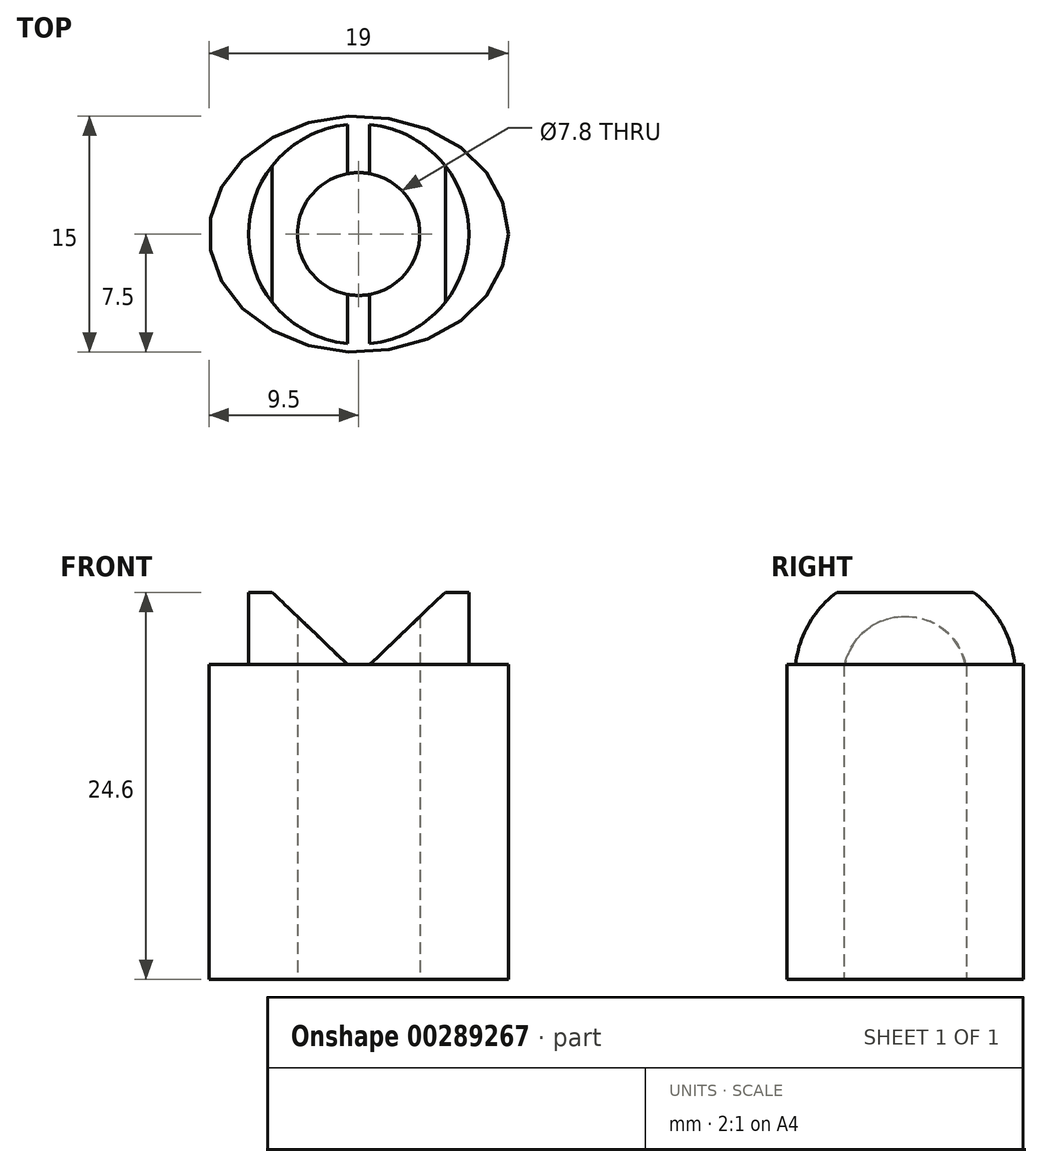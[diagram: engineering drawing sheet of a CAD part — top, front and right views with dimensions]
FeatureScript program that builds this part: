
annotation { "Feature Type Name" : "Feature", "Feature Type Description" : "" }
export const myFeature = defineFeature(function(context is Context, id is Id, definition is map)
    precondition{}
    {
        {
            var Q0;
            Q0=qCreatedBy(makeId("Top.planeOp"),FACE);
            var sketch = newSketch(context, id + "F0", { "sketchPlane" : qUnion([Q0])});
            skEllipse(sketch, "E0", {"center": v(0, 0) * mm, "majorRadius": 9.5 * mm, "minorRadius": 7.5 * mm, "majorAxis": v(1, 0)});
            skSolve(sketch);
        }
        {
            var Q0;
            Q0=makeQuery(id+"F0.imprint","IMPRINT",FACE,{"disambiguationData":[TD([[makeQuery(id+"F0.imprint","IMPRINT",EDGE,{"derivedFrom":sQuery(id+"F0.wireOp",EDGE,"E0")}),1.0]])]});
            extrude(context, id + "F1", {"entities" : qUnion([Q0]), "depth" : 20 * mm});
        }
        {
            var Q0;
            Q0=makeQuery(id+"F1.opExtrude","CAP_FACE",FACE,{"disambiguationData":[OSD([sQuery(id+"F0.wireOp",EDGE,"E0")])],"isStart":false});
            var sketch = newSketch(context, id + "F2", { "sketchPlane" : qUnion([Q0])});
            skCircle(sketch, "E1", {"center": v(0, 0) * mm, "radius": 7 * mm});
            skSolve(sketch);
        }
        {
            var Q0;
            Q0=makeQuery(id+"F2.imprint","IMPRINT",FACE,{"disambiguationData":[TD([[makeQuery(id+"F2.imprint","IMPRINT",EDGE,{"derivedFrom":sQuery(id+"F2.wireOp",EDGE,"E1")}),1.0]])]});
            extrude(context, id + "F3", {"entities" : qUnion([Q0]), "operationType" : NewBodyOperationType.ADD, "depth" : 4.6 * mm});
        }
        {
            var Q0;
            Q0=qCreatedBy(makeId("Front.planeOp"),FACE);
            var sketch = newSketch(context, id + "F4", { "sketchPlane" : qUnion([Q0])});
            skLineSegment(sketch, "E2.bottom", {"start": v(-0.7, 20) * mm, "end": v(0.7, 20) * mm});
            skLineSegment(sketch, "E2.top", {"start": v(-0.7, 24.6) * mm, "end": v(0.7, 24.6) * mm});
            skLineSegment(sketch, "E3.top", {"start": v(-5.5, 24.6) * mm, "end": v(5.5, 24.6) * mm});
            skLineSegment(sketch, "E4", {"start": v(-0.7, 20) * mm, "end": v(-5.5, 24.6) * mm});
            skLineSegment(sketch, "E5", {"start": v(5.5, 24.6) * mm, "end": v(0.7, 20) * mm});
            skSolve(sketch);
        }
        {
            var Q0;
            Q0 = qSketchRegion(id + "F4", true);
            extrude(context, id + "F5", {"entities" : qUnion([Q0]), "operationType" : NewBodyOperationType.REMOVE, "endBound" : BoundingType.SYMMETRIC, "depth" : 25 * mm});
        }
        {
            var Q0;
            Q0=makeQuery(id+"F1.opExtrude","CAP_FACE",FACE,{"disambiguationData":[OSD([sQuery(id+"F0.wireOp",EDGE,"E0")])],"isStart":true});
            var sketch = newSketch(context, id + "F6", { "sketchPlane" : qUnion([Q0])});
            skCircle(sketch, "E6", {"center": v(0, 0) * mm, "radius": 3.9 * mm});
            skSolve(sketch);
        }
        {
            var Q0;
            Q0 = qSketchRegion(id + "F6", true);
            extrude(context, id + "F7", {"entities" : qUnion([Q0]), "operationType" : NewBodyOperationType.REMOVE, "endBound" : BoundingType.THROUGH_ALL, "oppositeDirection" : true, "depth" : 25 * mm});
        }
    });
